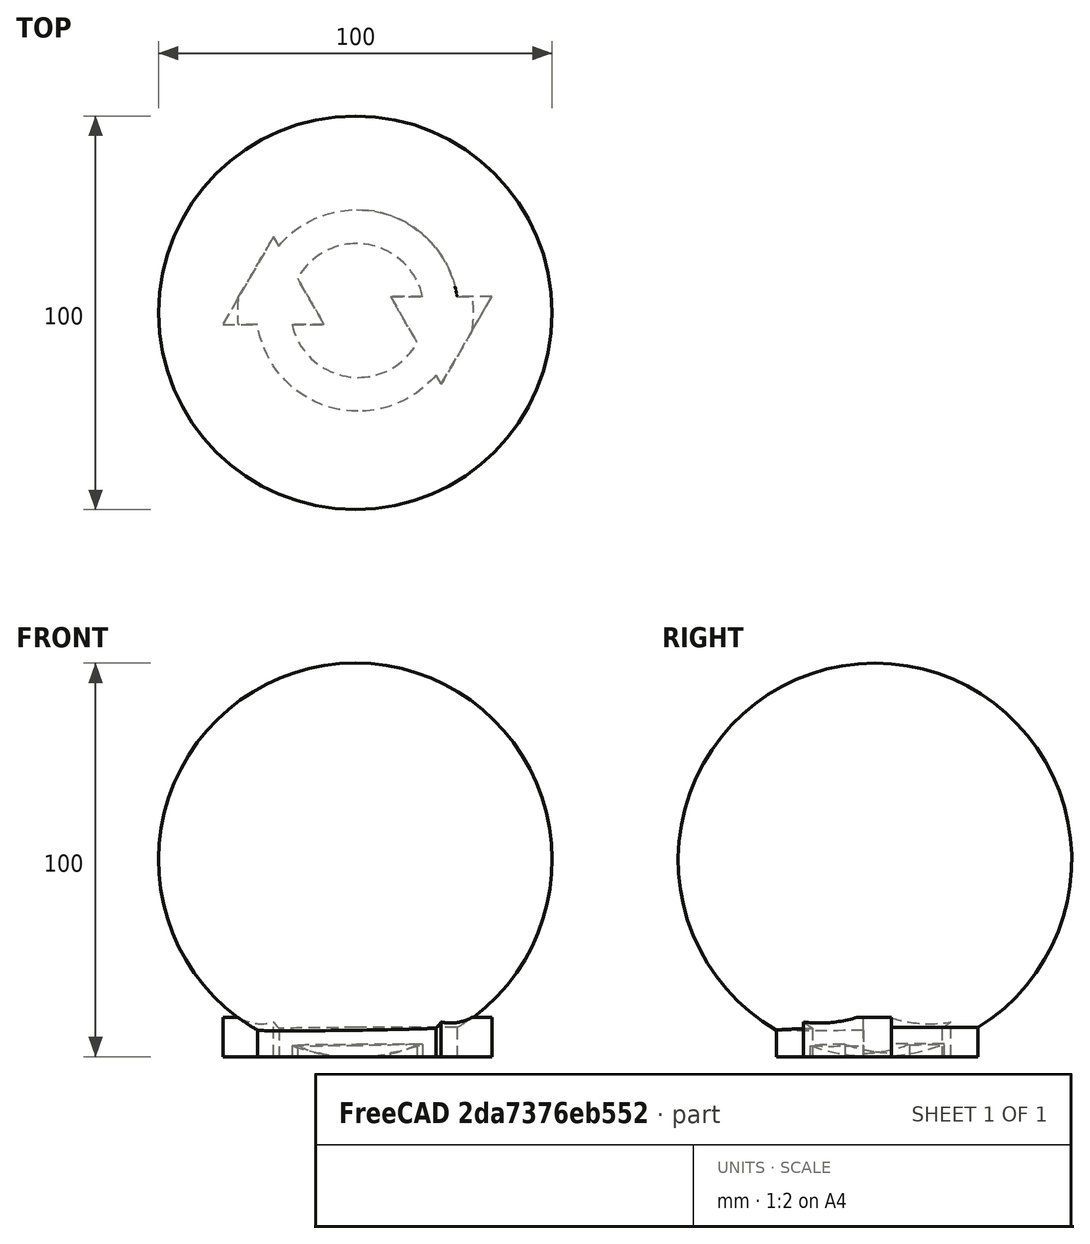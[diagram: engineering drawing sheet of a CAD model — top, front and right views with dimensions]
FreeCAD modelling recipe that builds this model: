
FCSTD DOCUMENT  (FreeCAD 0.15R4671 (Git))
Label: rotating_sphere
License: All rights reserved
LicenseURL: http://en.wikipedia.org/wiki/All_rights_reserved
objects: Part::Feature×4, Part::Extrusion×4, Part::MultiFuse×2, Part::Sphere×1, Mesh::Feature×1
note: 11 computed .brp shape members not serialized (recipe doc carries the construction recipe); baked Part::Feature solids carry a one-line shape summary decoded from their .brp

FEATURE [Part::Sphere] Sphere
  Angle1 = -90
  Angle2 = 90
  Angle3 = 360
  Placement = pos=(0,0,50) rot=(0,0,1;0rad)
  Radius = 50
FEATURE [Part::Feature] Face
  Placement = pos=(-41,37,0) rot=(0,0,1;0rad)
  shape: bbox 51.63 x 25.82 x 2e-07 mm, 1 faces, 0 solids (baked)
FEATURE [Part::Feature] Face001
  Placement = pos=(-41,37,0) rot=(0,0,1;0rad)
  shape: bbox 25.74 x 22.29 x 2e-07 mm, 1 faces, 0 solids (baked)
FEATURE [Part::Feature] Face002
  Placement = pos=(-41,37,0) rot=(0,0,1;0rad)
  shape: bbox 51.63 x 25.82 x 2e-07 mm, 1 faces, 0 solids (baked)
FEATURE [Part::Feature] Face003
  Placement = pos=(-41,37,0) rot=(0,0,1;0rad)
  shape: bbox 25.74 x 22.29 x 2e-07 mm, 1 faces, 0 solids (baked)
FEATURE [Part::Extrusion] Extrude
  Base = -> Face
  Dir = (0,0,10)
  Solid = false
FEATURE [Part::Extrusion] Extrude001
  Base = -> Face001
  Dir = (0,0,10)
  Solid = false
FEATURE [Part::Extrusion] Extrude002
  Base = -> Face002
  Dir = (0,0,10)
  Solid = false
FEATURE [Part::Extrusion] Extrude003
  Base = -> Face003
  Dir = (0,0,10)
  Solid = false
FEATURE [Part::MultiFuse] Fusion
  Shapes = -> [Extrude,Extrude001,Extrude003,Extrude002]
FEATURE [Part::MultiFuse] Fusion001
  Shapes = -> [Sphere,Fusion]
FEATURE [Mesh::Feature] Mesh  label="Fusion001 (Meshed)"
